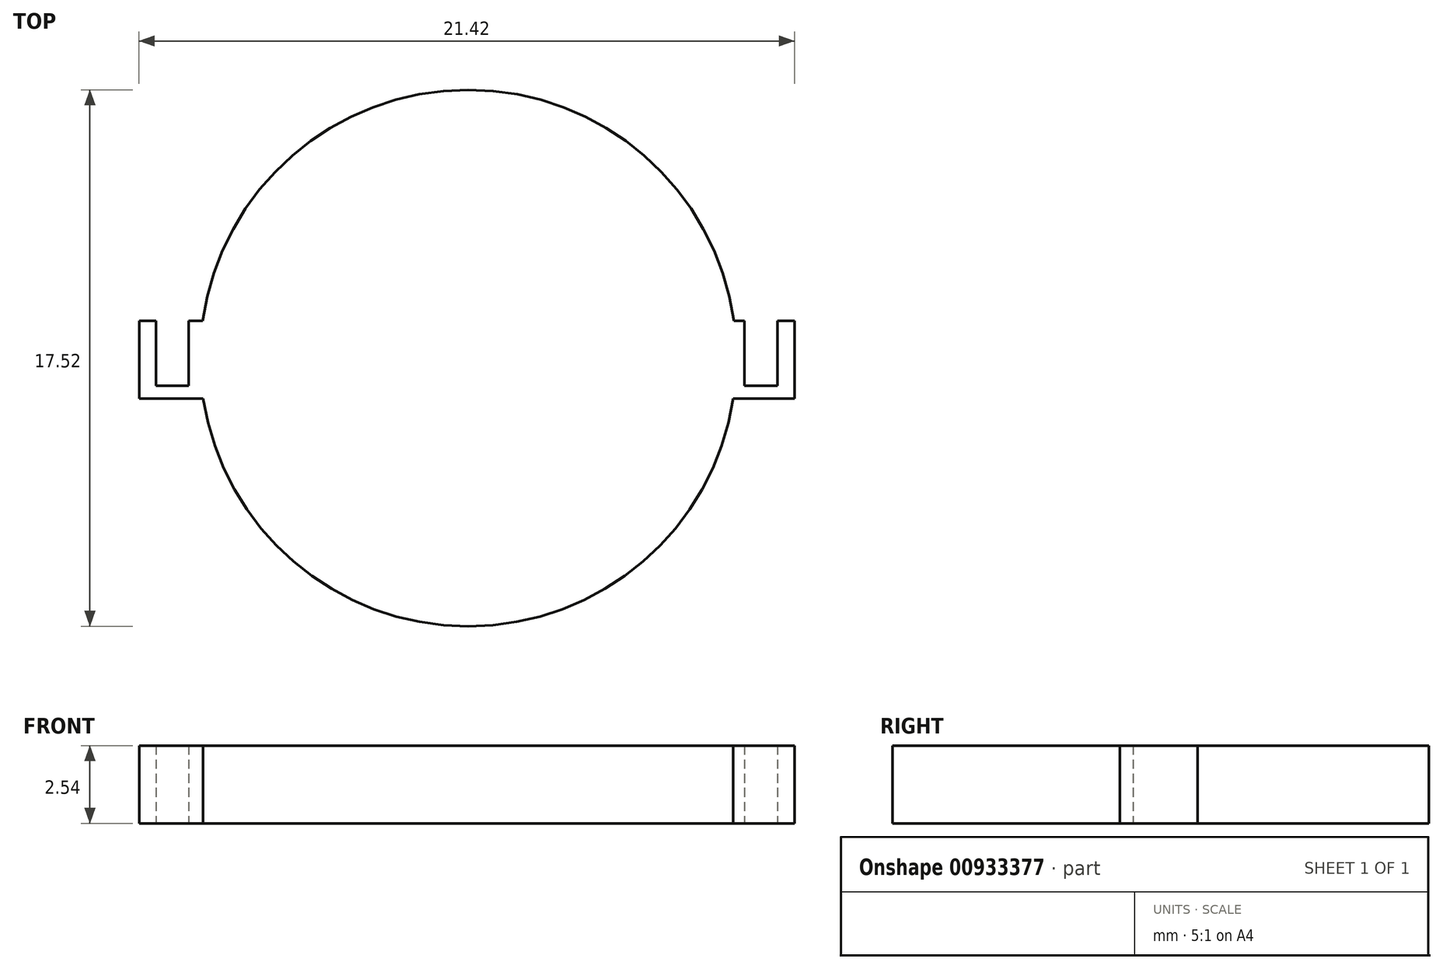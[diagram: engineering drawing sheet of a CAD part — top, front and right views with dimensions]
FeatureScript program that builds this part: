
annotation { "Feature Type Name" : "Feature", "Feature Type Description" : "" }
export const myFeature = defineFeature(function(context is Context, id is Id, definition is map)
    precondition{}
    {
        {
            var Q0;
            Q0=qCreatedBy(makeId("Top.planeOp"),FACE);
            var sketch = newSketch(context, id + "F0", { "sketchPlane" : qUnion([Q0])});
            skCircle(sketch, "E0", {"center": v(0, 0) * mm, "radius": 8.76 * mm});
            skLineSegment(sketch, "E1", {"start": v(-10.76, 1.21) * mm, "end": v(10.66, 1.21) * mm});
            skLineSegment(sketch, "E2", {"start": v(-10.76, -1.33) * mm, "end": v(10.66, -1.33) * mm});
            skLineSegment(sketch, "E3", {"start": v(10.66, -1.33) * mm, "end": v(10.66, 1.21) * mm});
            skLineSegment(sketch, "E4", {"start": v(-10.76, -1.33) * mm, "end": v(-10.76, 1.21) * mm});
            skLineSegment(sketch, "E5", {"start": v(-10.2, 1.16) * mm, "end": v(-10.2, -0.9) * mm});
            skLineSegment(sketch, "E6", {"start": v(-10.2, -0.9) * mm, "end": v(-9.13, -0.9) * mm});
            skLineSegment(sketch, "E7", {"start": v(-9.13, -0.9) * mm, "end": v(-9.13, 1.54) * mm});
            skLineSegment(sketch, "E8", {"start": v(-9.13, 1.16) * mm, "end": v(-9.13, 1.54) * mm});
            skLineSegment(sketch, "E9", {"start": v(9.03, 1.54) * mm, "end": v(9.03, -0.9) * mm});
            skLineSegment(sketch, "E10", {"start": v(9.03, -0.9) * mm, "end": v(10.1, -0.9) * mm});
            skLineSegment(sketch, "E11", {"start": v(10.1, -0.9) * mm, "end": v(10.1, 1.54) * mm});
            skLineSegment(sketch, "E12", {"start": v(-10.2, 1.16) * mm, "end": v(-10.2, 1.4) * mm});
            skSolve(sketch);
        }
        {
            var Q0;
            {var subQ0=sQuery(id+"F0.wireOp",EDGE,"E1");var subQ1=sQuery(id+"F0.wireOp",EDGE,"E0");var subQ2=makeQuery(id+"F0.imprint","INTERSECT",VERTEX,{"disambiguationData":[OD(0.0)],"derivedFrom":[subQ1,subQ0]});Q0=makeQuery(id+"F0.imprint","IMPRINT",FACE,{"disambiguationData":[TD([[makeQuery(id+"F0.imprint","IMPRINT",EDGE,{"disambiguationData":[TD([[subQ2,1.0]])],"derivedFrom":subQ1}),1.0]])]});}
            var Q1;
            {var subQ0=sQuery(id+"F0.wireOp",EDGE,"E1");var subQ1=sQuery(id+"F0.wireOp",EDGE,"E0");var subQ2=makeQuery(id+"F0.imprint","INTERSECT",VERTEX,{"disambiguationData":[OD(0.0)],"derivedFrom":[subQ1,subQ0]});Q1=makeQuery(id+"F0.imprint","IMPRINT",FACE,{"disambiguationData":[TD([[makeQuery(id+"F0.imprint","IMPRINT",EDGE,{"disambiguationData":[TD([[subQ2,-1.0]])],"derivedFrom":subQ1}),1.0]])]});}
            var Q2;
            {var subQ0=sQuery(id+"F0.wireOp",EDGE,"E2");var subQ1=sQuery(id+"F0.wireOp",EDGE,"E0");var subQ2=makeQuery(id+"F0.imprint","INTERSECT",VERTEX,{"disambiguationData":[OD(0.0)],"derivedFrom":[subQ1,subQ0]});Q2=makeQuery(id+"F0.imprint","IMPRINT",FACE,{"disambiguationData":[TD([[makeQuery(id+"F0.imprint","IMPRINT",EDGE,{"disambiguationData":[TD([[subQ2,-1.0]])],"derivedFrom":subQ1}),1.0]])]});}
            var Q3;
            {var subQ0=sQuery(id+"F0.wireOp",EDGE,"E3");Q3=makeQuery(id+"F0.imprint","IMPRINT",FACE,{"disambiguationData":[TD([[makeQuery(id+"F0.imprint","IMPRINT",EDGE,{"derivedFrom":subQ0}),1.0]])]});}
            var Q4;
            {var subQ0=sQuery(id+"F0.wireOp",EDGE,"E4");Q4=makeQuery(id+"F0.imprint","IMPRINT",FACE,{"disambiguationData":[TD([[makeQuery(id+"F0.imprint","IMPRINT",EDGE,{"derivedFrom":subQ0}),-1.0]])]});}
            extrude(context, id + "F1", {"entities" : qUnion([Q0, Q1, Q2, Q3, Q4]), "depth" : 2.54 * mm, "offsetDistance" : 25.4 * mm});
        }
    });
